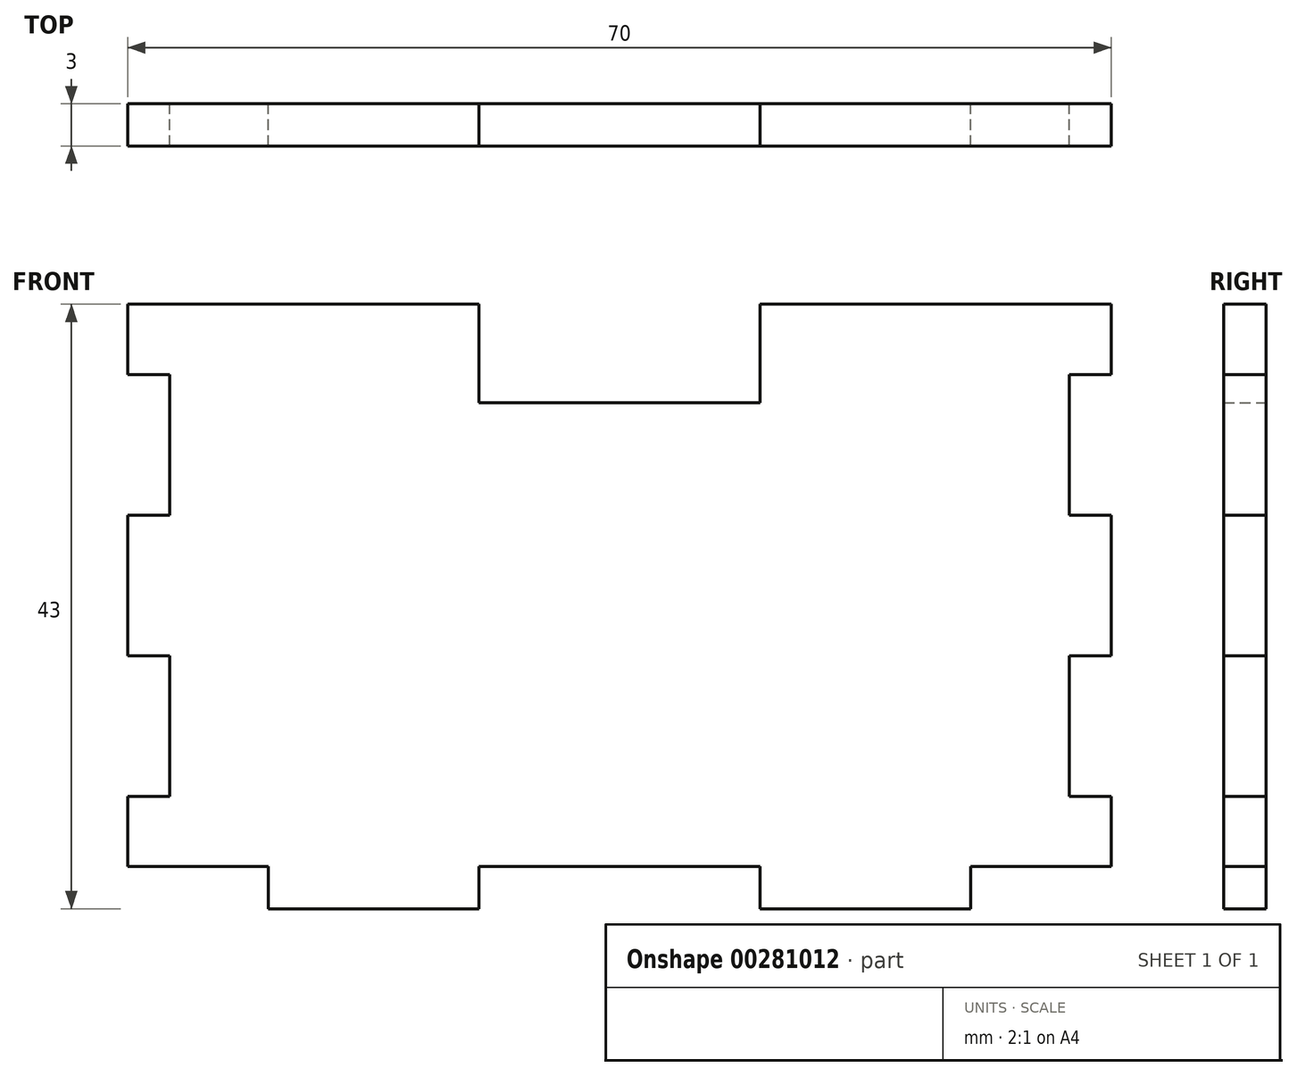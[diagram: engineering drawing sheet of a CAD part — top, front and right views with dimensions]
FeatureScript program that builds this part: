
annotation { "Feature Type Name" : "Feature", "Feature Type Description" : "" }
export const myFeature = defineFeature(function(context is Context, id is Id, definition is map)
    precondition{}
    {
        {
            var Q0;
            Q0=qCreatedBy(makeId("Front.planeOp"),FACE);
            var sketch = newSketch(context, id + "F0", { "sketchPlane" : qUnion([Q0])});
            skLineSegment(sketch, "E0.bottom", {"start": v(35, -20) * mm, "end": v(25, -20) * mm});
            skLineSegment(sketch, "E0.top", {"start": v(35, 20) * mm, "end": v(10, 20) * mm});
            skLineSegment(sketch, "E0.right", {"start": v(-35, -20) * mm, "end": v(-35, -15) * mm});
            skPoint(sketch, "E0.middle", {"position": v(0, 0) * mm});
            skLineSegment(sketch, "E1.top", {"start": v(-10, -23) * mm, "end": v(-25, -23) * mm});
            skLineSegment(sketch, "E1.left", {"start": v(-10, -20) * mm, "end": v(-10, -23) * mm});
            skLineSegment(sketch, "E1.right", {"start": v(-25, -20) * mm, "end": v(-25, -23) * mm});
            skLineSegment(sketch, "E2.top", {"start": v(10, -23) * mm, "end": v(25, -23) * mm});
            skLineSegment(sketch, "E2.left", {"start": v(10, -20) * mm, "end": v(10, -23) * mm});
            skLineSegment(sketch, "E2.right", {"start": v(25, -20) * mm, "end": v(25, -23) * mm});
            skLineSegment(sketch, "E3.trimOffspring", {"start": v(-25, -20) * mm, "end": v(-35, -20) * mm});
            skLineSegment(sketch, "E4.trimOffspring", {"start": v(10, -20) * mm, "end": v(-10, -20) * mm});
            skLineSegment(sketch, "E5.bottom", {"start": v(-35, 15) * mm, "end": v(-32, 15) * mm});
            skLineSegment(sketch, "E5.top", {"start": v(-35, 5) * mm, "end": v(-32, 5) * mm});
            skLineSegment(sketch, "E5.right", {"start": v(-32, 15) * mm, "end": v(-32, 5) * mm});
            skLineSegment(sketch, "E6.bottom", {"start": v(-35, -5) * mm, "end": v(-32, -5) * mm});
            skLineSegment(sketch, "E6.top", {"start": v(-35, -15) * mm, "end": v(-32, -15) * mm});
            skLineSegment(sketch, "E6.right", {"start": v(-32, -5) * mm, "end": v(-32, -15) * mm});
            skLineSegment(sketch, "E7.trimOffspring", {"start": v(-35, 15) * mm, "end": v(-35, 20) * mm});
            skLineSegment(sketch, "E8.trimOffspring", {"start": v(-35, -5) * mm, "end": v(-35, 5) * mm});
            skLineSegment(sketch, "E9.MirrorCS", {"start": v(35, 5) * mm, "end": v(32, 5) * mm});
            skLineSegment(sketch, "E10.MirrorCS", {"start": v(35, 15) * mm, "end": v(32, 15) * mm});
            skLineSegment(sketch, "E11.MirrorCS", {"start": v(35, -5) * mm, "end": v(32, -5) * mm});
            skLineSegment(sketch, "E12.MirrorCS", {"start": v(35, -15) * mm, "end": v(32, -15) * mm});
            skLineSegment(sketch, "E13.MirrorCS", {"start": v(35, -5) * mm, "end": v(35, 5) * mm});
            skLineSegment(sketch, "E14.MirrorCS", {"start": v(32, -5) * mm, "end": v(32, -15) * mm});
            skLineSegment(sketch, "E15.MirrorCS", {"start": v(32, 15) * mm, "end": v(32, 5) * mm});
            skLineSegment(sketch, "E16.MirrorCS", {"start": v(35, 15) * mm, "end": v(35, 20) * mm});
            skLineSegment(sketch, "E17.MirrorCS", {"start": v(35, -20) * mm, "end": v(35, -15) * mm});
            skLineSegment(sketch, "E18.top", {"start": v(-10, 13) * mm, "end": v(10, 13) * mm});
            skLineSegment(sketch, "E18.left", {"start": v(-10, 20) * mm, "end": v(-10, 13) * mm});
            skLineSegment(sketch, "E18.right", {"start": v(10, 20) * mm, "end": v(10, 13) * mm});
            skLineSegment(sketch, "E19.trimOffspring", {"start": v(-10, 20) * mm, "end": v(-35, 20) * mm});
            skSolve(sketch);
        }
        {
            var Q0;
            Q0 = qSketchRegion(id + "F0", true);
            extrude(context, id + "F1", {"entities" : qUnion([Q0]), "depth" : 3 * mm});
        }
    });
